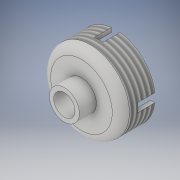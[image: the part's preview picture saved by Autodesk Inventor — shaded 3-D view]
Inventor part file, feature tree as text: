
AUTODESK INVENTOR PART (.ipt)
format: ipt  version: 2019 (Build 230136000, 136)  size: 174,080 bytes
history: native  units: mm
features: extrude x6, sketch x4, plane x2, fillet x1, thread x1
ambient origin geometry x8: Origin, YZ Plane, XZ Plane, XY Plane, X Axis, Y Axis, Z Axis, Center Point
bodies: Solid1 (feature_tree)
feature tree (14):
  sketch  "Sketch1"  dims[d0=82.0mm d1=25.0mm d2=92.0mm]
  extrude  "Extrusion1"  Depth=25.0mm
  fillet  "Fillet1"  Radius=92.0mm
  extrude  "Extrusion2"  Depth=10.0mm
  extrude  "Extrusion3"  Depth=33.0mm
  extrude  "Extrusion4"  Depth=40.0mm TaperAngle=0.0deg
  thread  "Thread1"  [1 undecoded]
  plane  "Work Plane1"
  plane  "Work Plane2"
  extrude  "Extrusion5"  Depth=10.0mm
  extrude  "Extrusion6"  Depth=40.0mm
  sketch  "Sketch2"  dims[d3=40.0mm d4=0.0mm d5=10.0mm]
  sketch  "Sketch3"  dims[d6=33.0mm d7=0.0mm d8=35.0mm]
  sketch  "Sketch4"  dims[d9=20.0mm d10=0.0mm d11=118.5mm d12=0.0mm d13=20.0mm d14=0.0mm d15=10.0mm d16=40.0mm d17=154.5mm d18=0.0mm d19=10.0mm d20=40.0mm d21=154.5mm d22=0.0mm]
note: 1 required parameter value undecoded (feature->parameter linkage not recoverable at this tier; creation-order binding heuristic only, values carry confidence <= 0.55)
